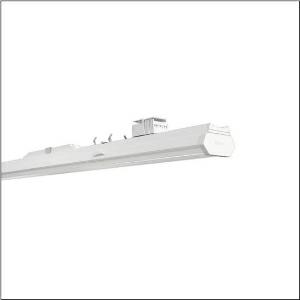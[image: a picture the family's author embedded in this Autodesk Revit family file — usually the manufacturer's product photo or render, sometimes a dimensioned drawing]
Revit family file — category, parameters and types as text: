
# Revit family: licross_r__11_protected_mo_51td1bdn68xg3s_e11a
name_source: partatom
category: Lighting Fixtures
units: mm (PartAtom-declared; Revit-internal decimal feet)

## family parameters
Cut with Voids When Loaded = No
Host = Face
Light Source = No
Part Type = Normal
Room Calculation Point = No
Round Connector Dimension = Use Diameter
Shared = No

## types (1)
- --- (1 x LED, 900 lm, 6.8 W, 6500K)
    Apparent Load = 7 VA
    CIE Flux Codes = 54 82 95 97 100
    Color Rendering = 80
    Color Temperature = 6500K
    Default Elevation = 1800 mm
    Description = Licross® 11 Protected MO, luminaire insert, of sheet steel, galvanised, coil coated, white, length: 1.500mm, width: 90mm, height: 101mm, LED rated luminous flux: 8.310lm, light colour: 865, control gear: DALI 2 (for two DALI lines), with plug, 6-pole, with phase selection, for trunking rail, 14-core, mains connection: 220..240V, AC, 50/60Hz, rated input power: 55W, for trunking rail, 14-core, internal wiring halogen-free, for emergency light function, converter,control gear: single battery element, battery: LiFePO4, 9Ah, primary optical cover: cover, of PMMA, light emission: direct distribution, primary light characteristic: symmetric, protection rating (complete): IP54, insulation class (complete): insulation class I (protective earthing), certification: CE, UKCA, protection symbol: D if used in an environment with non-conductive dust loads with corresponding accessories, impact resistance: IK06, permissible ambient temperature for indoor applications: +5..+35°C, standard: EN 60598-2-22, corresponds to IFS (International Featured Standards) requirements for safety and quality in the food industry, reducing of maximum allowable ambient temperature of 5°C with ceiling mounting, LABS conformity tested according to VDMA 24364:2018-05, packaging unit: 1 piece
    Height = 92 mm
    Lamp = 1 x LED
    Lamp Light Flux = 900 lm
    Lamp Power = 6.8 W
    Lamp count = 1
    Length = 1500 mm
    Luminous efficacy = 132 lm/W
    Manufacturer = Siteco
    ModVariant = No
    Model = 51TD1BDN68XG3S
    Mounting Place = Ceiling
    Mounting Type = Pendant
    Number of Poles = 1
    OnlyDefault = Yes
    Power Factor = 1
    Product Name = Licross® 11 Protected MO
    Product group = luminaire insert | ceiling pendant
    ProductGroupID = 902
    Protection Class = Protection class I
    Protection Degree = IP 54
    RLX_Detail_Level = 1
    RLX_Emergency_Light_Flux = 0 lm
    RLX_Emergency_Type = 0
    RLX_Emergency_Type_DB = No
    RlxData = <blob elided: 24797 chars, md5=e5433339>
    Socket = socket
    Standby Power = 0 W
    System Light Flux = 900 lm
    System Power = 7 W
    Type Comments = : emergency light operation: 3 h
    Type Image = l_1256145.jpg
    URL = http://relux.com
    VarID = @adj_051531
    Voltage = 0 V
    Weight = 0.00 kg
    Width = 88 mm

## geometry (parser evidence)
native form markers: Blend x4, Sweep x10
no freeform markers — native parametric forms only
